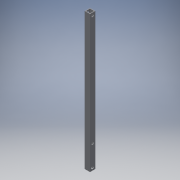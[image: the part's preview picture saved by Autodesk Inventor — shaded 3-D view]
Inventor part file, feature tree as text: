
AUTODESK INVENTOR PART (.ipt)
format: ipt  version: 2016 (Build 200138000, 138)  size: 135,168 bytes
history: native  units: in
note: dims shown in document units (in); Inventor stores cm internally (conversion verified against a paired STEP export)
features: sketch x5, extrude x4
ambient origin geometry x8: Origin, YZ Plane, XZ Plane, XY Plane, X Axis, Y Axis, Z Axis, Center Point
bodies: Solid1 (feature_tree)
feature tree (9):
  extrude  "Extrusion1"  Depth=1.0in
  extrude  "Extrusion2"  Depth=0.125in
  extrude  "Extrusion3"  Depth=0.125in
  sketch  "Sketch4"  dims[d7=26.0in d8=0.0in d9=0.5in]
  extrude  "Extrusion4"  Depth=26.0in
  sketch  "Sketch1"  dims[d0=1.0in d1=1.0in]
  sketch  "Sketch2"  dims[d2=0.125in d4=0.125in]
  sketch  "Sketch3"  dims[d5=0.125in d6=0.125in]
  sketch  "Sketch5"  dims[d10=0.5in d11=0.5in d12=0.5in d13=0.5in d14=0.5in d15=26.0in d16=0.0in d17=0.5in d18=0.5in d19=0.5in d20=0.5in d21=4.0in d22=0.5in d23=26.0in d24=0.0in d25=0.5in d26=4.0in d27=0.5in d28=26.0in d29=0.0in]
